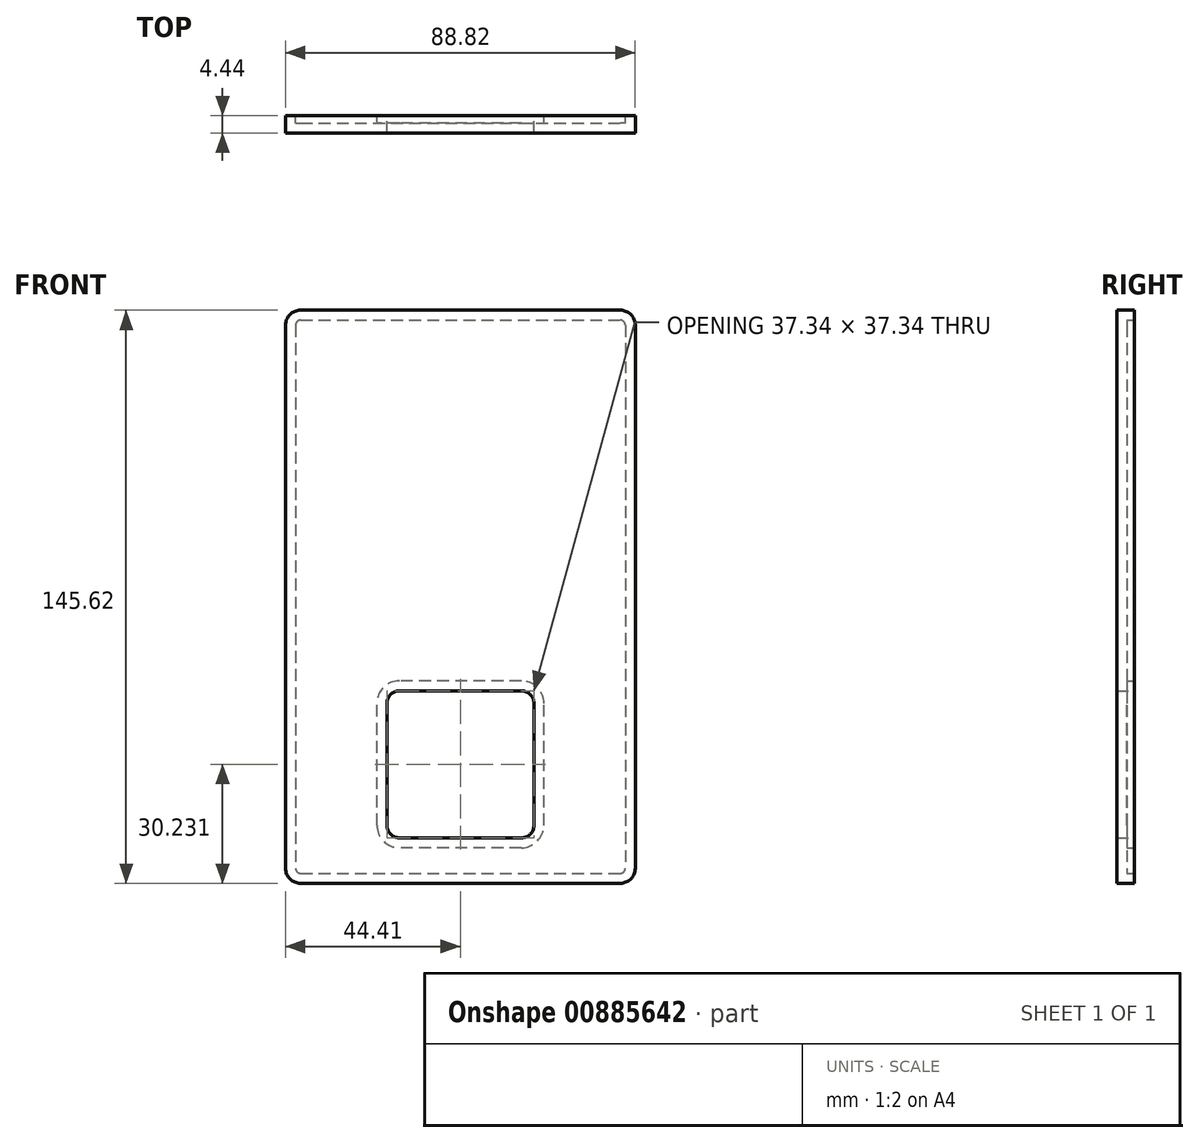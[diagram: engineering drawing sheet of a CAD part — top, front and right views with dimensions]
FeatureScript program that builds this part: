
annotation { "Feature Type Name" : "Feature", "Feature Type Description" : "" }
export const myFeature = defineFeature(function(context is Context, id is Id, definition is map)
    precondition{}
    {
        {
            var Q0;
            Q0=qCreatedBy(makeId("Front.planeOp"),FACE);
            var sketch = newSketch(context, id + "F0", { "sketchPlane" : qUnion([Q0])});
            skLineSegment(sketch, "E0.bottom", {"start": v(-40.6, 72.8) * mm, "end": v(40.6, 72.8) * mm});
            skLineSegment(sketch, "E0.top", {"start": v(-40.6, -72.8) * mm, "end": v(40.6, -72.8) * mm});
            skLineSegment(sketch, "E0.left", {"start": v(-44.41, 69) * mm, "end": v(-44.41, -69) * mm});
            skLineSegment(sketch, "E0.right", {"start": v(44.41, 69) * mm, "end": v(44.41, -69) * mm});
            skPoint(sketch, "E0.middle", {"position": v(0, 0) * mm});
            skPoint(sketch, "E1.visualSharp", {"position": v(-44.41, -72.8) * mm});
            skArc(sketch, "E1.filletArc", {"start": v(-44.41, -69) * mm, "mid": v(-43.3, -71.7) * mm, "end": v(-40.6, -72.8) * mm});
            skPoint(sketch, "E2.visualSharp", {"position": v(44.41, -72.8) * mm});
            skArc(sketch, "E2.filletArc", {"start": v(40.6, -72.8) * mm, "mid": v(43.3, -71.7) * mm, "end": v(44.41, -69) * mm});
            skPoint(sketch, "E3.visualSharp", {"position": v(44.41, 72.8) * mm});
            skArc(sketch, "E3.filletArc", {"start": v(44.41, 69) * mm, "mid": v(43.3, 71.7) * mm, "end": v(40.6, 72.8) * mm});
            skPoint(sketch, "E4.visualSharp", {"position": v(-44.41, 72.8) * mm});
            skArc(sketch, "E4.filletArc", {"start": v(-40.6, 72.8) * mm, "mid": v(-43.3, 71.7) * mm, "end": v(-44.41, 69) * mm});
            skSolve(sketch);
        }
        {
            var Q0;
            Q0=makeQuery(id+"F0.imprint","IMPRINT",FACE,{"disambiguationData":[TD([[makeQuery(id+"F0.imprint","IMPRINT",EDGE,{"derivedFrom":sQuery(id+"F0.wireOp",EDGE,"E0.bottom")}),-1.0]])]});
            var sketch = newSketch(context, id + "F1", { "sketchPlane" : qUnion([Q0])});
            skLineSegment(sketch, "E5.bottom", {"start": v(-15.5, -23.9) * mm, "end": v(15.5, -23.9) * mm});
            skLineSegment(sketch, "E5.top", {"start": v(-15.5, -61.25) * mm, "end": v(15.5, -61.25) * mm});
            skLineSegment(sketch, "E5.left", {"start": v(-18.67, -27.08) * mm, "end": v(-18.67, -58.07) * mm});
            skLineSegment(sketch, "E5.right", {"start": v(18.67, -27.08) * mm, "end": v(18.67, -58.07) * mm});
            skPoint(sketch, "E5.middle", {"position": v(0, -42.58) * mm});
            skPoint(sketch, "E6.visualSharp", {"position": v(-18.67, -23.9) * mm});
            skArc(sketch, "E6.filletArc", {"start": v(-15.5, -23.9) * mm, "mid": v(-17.74, -24.84) * mm, "end": v(-18.67, -27.08) * mm});
            skPoint(sketch, "E7.visualSharp", {"position": v(18.67, -23.9) * mm});
            skArc(sketch, "E7.filletArc", {"start": v(18.67, -27.08) * mm, "mid": v(17.74, -24.84) * mm, "end": v(15.5, -23.9) * mm});
            skPoint(sketch, "E8.visualSharp", {"position": v(-18.67, -61.25) * mm});
            skArc(sketch, "E8.filletArc", {"start": v(-18.67, -58.07) * mm, "mid": v(-17.74, -60.32) * mm, "end": v(-15.5, -61.25) * mm});
            skPoint(sketch, "E9.visualSharp", {"position": v(18.67, -61.25) * mm});
            skArc(sketch, "E9.filletArc", {"start": v(15.5, -61.25) * mm, "mid": v(17.74, -60.32) * mm, "end": v(18.67, -58.07) * mm});
            skSolve(sketch);
        }
        {
            var Q0;
            Q0 = qSketchRegion(id + "F0", true);
            extrude(context, id + "F2", {"entities" : qUnion([Q0]), "endBound" : BoundingType.SYMMETRIC, "depth" : 4.44 * mm, "offsetDistance" : 25.4 * mm});
        }
        {
            var Q0;
            Q0 = qSketchRegion(id + "F1", true);
            extrude(context, id + "F3", {"entities" : qUnion([Q0]), "operationType" : NewBodyOperationType.REMOVE, "endBound" : BoundingType.SYMMETRIC, "depth" : 25.4 * mm, "offsetDistance" : 25.4 * mm});
        }
        {
            var Q0;
            Q0=makeQuery(id+"F2.opExtrude","CAP_FACE",FACE,{"disambiguationData":[OSD([sQuery(id+"F0.wireOp",EDGE,"E0.bottom"),sQuery(id+"F0.wireOp",EDGE,"E0.top"),sQuery(id+"F0.wireOp",EDGE,"E0.left"),sQuery(id+"F0.wireOp",EDGE,"E0.right"),sQuery(id+"F0.wireOp",EDGE,"E1.filletArc"),sQuery(id+"F0.wireOp",EDGE,"E2.filletArc"),sQuery(id+"F0.wireOp",EDGE,"E3.filletArc"),sQuery(id+"F0.wireOp",EDGE,"E4.filletArc")])],"isStart":true});
            shell(context, id + "F4", {"entities" : qUnion([Q0]), "thickness" : 2.54 * mm});
        }
    });
